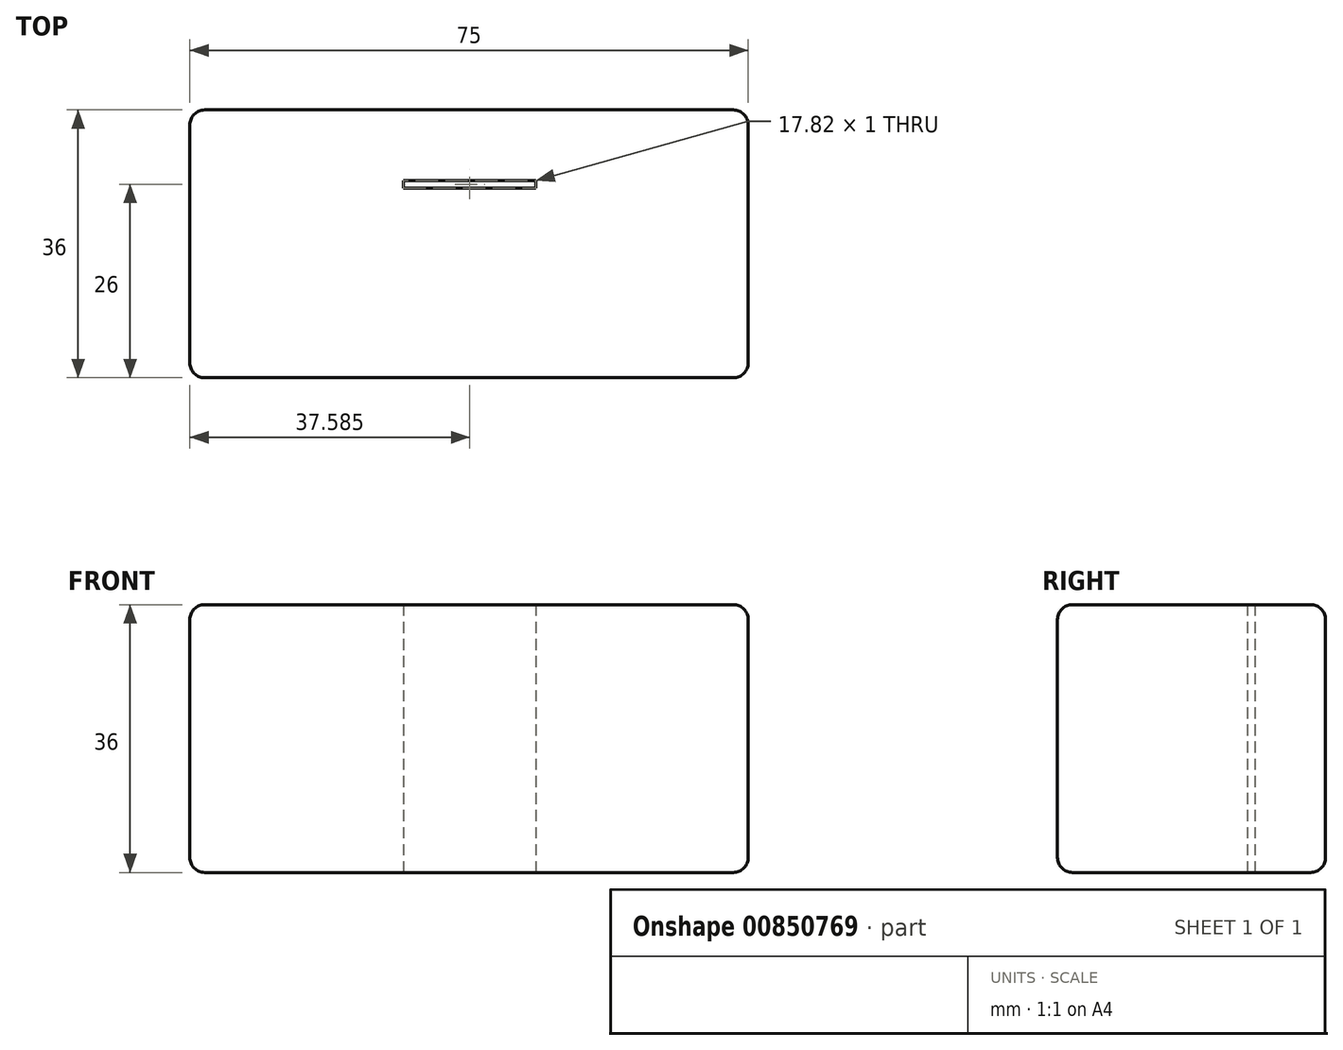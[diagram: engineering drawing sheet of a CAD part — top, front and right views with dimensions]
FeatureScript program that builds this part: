
annotation { "Feature Type Name" : "Feature", "Feature Type Description" : "" }
export const myFeature = defineFeature(function(context is Context, id is Id, definition is map)
    precondition{}
    {
        {
            var Q0;
            Q0=qCreatedBy(makeId("Top.planeOp"),FACE);
            var sketch = newSketch(context, id + "F0", { "sketchPlane" : qUnion([Q0])});
            skLineSegment(sketch, "E0.bottom", {"start": v(37.5, -18) * mm, "end": v(-37.5, -18) * mm});
            skLineSegment(sketch, "E0.top", {"start": v(37.5, 18) * mm, "end": v(-37.5, 18) * mm});
            skLineSegment(sketch, "E0.left", {"start": v(37.5, -18) * mm, "end": v(37.5, 18) * mm});
            skLineSegment(sketch, "E0.right", {"start": v(-37.5, -18) * mm, "end": v(-37.5, 18) * mm});
            skPoint(sketch, "E0.middle", {"position": v(0, 0) * mm});
            skLineSegment(sketch, "E1", {"start": v(-8.83, 8) * mm, "end": v(9, 8) * mm});
            skLineSegment(sketch, "E2.bottom", {"start": v(-8.83, 8.5) * mm, "end": v(9, 8.5) * mm});
            skLineSegment(sketch, "E2.top", {"start": v(-8.83, 7.5) * mm, "end": v(9, 7.5) * mm});
            skLineSegment(sketch, "E2.left", {"start": v(-8.83, 8.5) * mm, "end": v(-8.83, 7.5) * mm});
            skLineSegment(sketch, "E2.right", {"start": v(9, 8.5) * mm, "end": v(9, 7.5) * mm});
            skPoint(sketch, "E2.middle", {"position": v(0.09, 8) * mm});
            skSolve(sketch);
        }
        {
            var Q0;
            Q0=qSketchRegion(id+"F0",true);
            extrude(context, id + "F1", {"entities" : qUnion([Q0]), "depth" : 36 * mm, "offsetDistance" : 25 * mm});
        }
        {
            var Q0;
            Q0=makeQuery(id+"F1.opExtrude","CAP_EDGE",EDGE,{"disambiguationData":[OSD([sQuery(id+"F0.wireOp",EDGE,"E0.bottom")])],"isStart":false});
            var Q1;
            Q1=makeQuery(id+"F1.opExtrude","SWEPT_EDGE",EDGE,{"disambiguationData":[OSD([sQuery(id+"F0.wireOp",EDGE,"E0.bottom"),sQuery(id+"F0.wireOp",EDGE,"E0.left")])]});
            var Q2;
            Q2=makeQuery(id+"F1.opExtrude","CAP_EDGE",EDGE,{"disambiguationData":[OSD([sQuery(id+"F0.wireOp",EDGE,"E0.left")])],"isStart":false});
            var Q3;
            Q3=makeQuery(id+"F1.opExtrude","SWEPT_EDGE",EDGE,{"disambiguationData":[OSD([sQuery(id+"F0.wireOp",EDGE,"E0.top"),sQuery(id+"F0.wireOp",EDGE,"E0.left")])]});
            var Q4;
            Q4=makeQuery(id+"F1.opExtrude","CAP_EDGE",EDGE,{"disambiguationData":[OSD([sQuery(id+"F0.wireOp",EDGE,"E0.left")])],"isStart":true});
            var Q5;
            Q5=makeQuery(id+"F1.opExtrude","CAP_EDGE",EDGE,{"disambiguationData":[OSD([sQuery(id+"F0.wireOp",EDGE,"E0.bottom")])],"isStart":true});
            var Q6;
            Q6=makeQuery(id+"F1.opExtrude","SWEPT_EDGE",EDGE,{"disambiguationData":[OSD([sQuery(id+"F0.wireOp",EDGE,"E0.bottom"),sQuery(id+"F0.wireOp",EDGE,"E0.right")])]});
            var Q7;
            Q7=makeQuery(id+"F1.opExtrude","CAP_EDGE",EDGE,{"disambiguationData":[OSD([sQuery(id+"F0.wireOp",EDGE,"E0.top")])],"isStart":true});
            var Q8;
            Q8=makeQuery(id+"F1.opExtrude","CAP_EDGE",EDGE,{"disambiguationData":[OSD([sQuery(id+"F0.wireOp",EDGE,"E0.right")])],"isStart":true});
            var Q9;
            Q9=makeQuery(id+"F1.opExtrude","SWEPT_EDGE",EDGE,{"disambiguationData":[OSD([sQuery(id+"F0.wireOp",EDGE,"E0.top"),sQuery(id+"F0.wireOp",EDGE,"E0.right")])]});
            var Q10;
            Q10=makeQuery(id+"F1.opExtrude","CAP_EDGE",EDGE,{"disambiguationData":[OSD([sQuery(id+"F0.wireOp",EDGE,"E0.right")])],"isStart":false});
            var Q11;
            Q11=makeQuery(id+"F1.opExtrude","CAP_EDGE",EDGE,{"disambiguationData":[OSD([sQuery(id+"F0.wireOp",EDGE,"E0.top")])],"isStart":false});
            fillet(context, id + "F2", {"entities" : qUnion([Q0, Q1, Q2, Q3, Q4, Q5, Q6, Q7, Q8, Q9, Q10, Q11]), "radius" : 2 * mm, "tangentPropagation" : true, "allowEdgeOverflow" : false});
        }
    });
